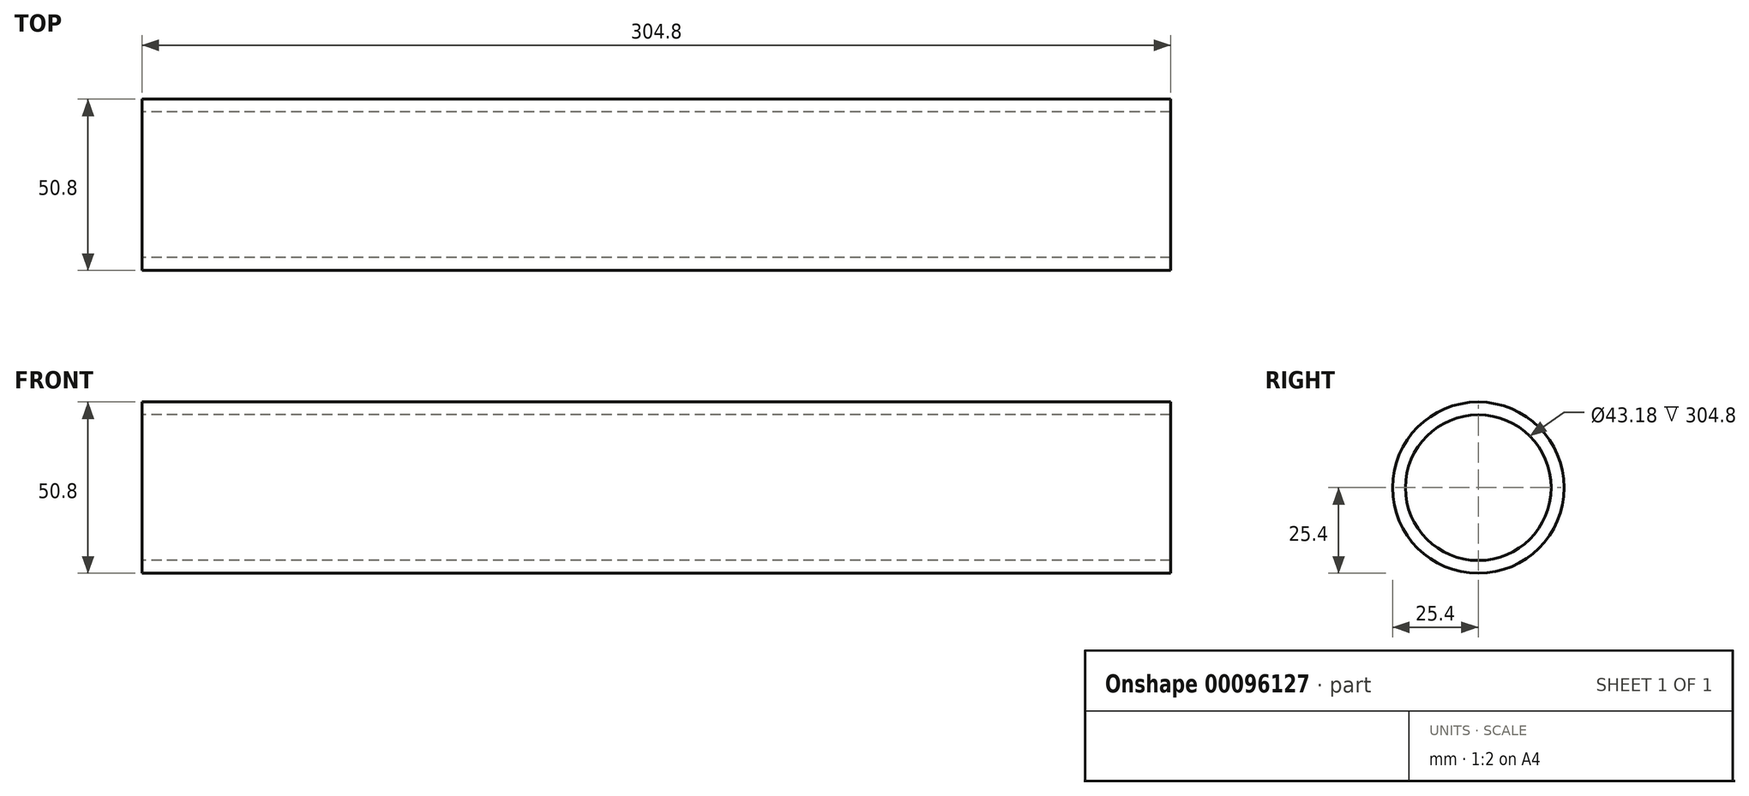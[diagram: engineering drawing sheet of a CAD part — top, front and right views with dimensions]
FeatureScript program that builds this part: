
annotation { "Feature Type Name" : "Feature", "Feature Type Description" : "" }
export const myFeature = defineFeature(function(context is Context, id is Id, definition is map)
    precondition{}
    {
        {
            var Q0;
            Q0=qCreatedBy(makeId("Right.planeOp"),FACE);
            var sketch = newSketch(context, id + "F0", { "sketchPlane" : qUnion([Q0])});
            skCircle(sketch, "E0", {"center": v(0, 0) * mm, "radius": 25.4 * mm});
            skCircle(sketch, "E1", {"center": v(0, 0) * mm, "radius": 21.59 * mm});
            skSolve(sketch);
        }
        {
            var Q0;
            Q0=makeQuery(id+"F0.imprint","IMPRINT",FACE,{"disambiguationData":[TD([[makeQuery(id+"F0.imprint","IMPRINT",EDGE,{"derivedFrom":sQuery(id+"F0.wireOp",EDGE,"E0")}),1.0]])]});
            extrude(context, id + "F1", {"entities" : qUnion([Q0]), "depth" : 304.8 * mm});
        }
    });
